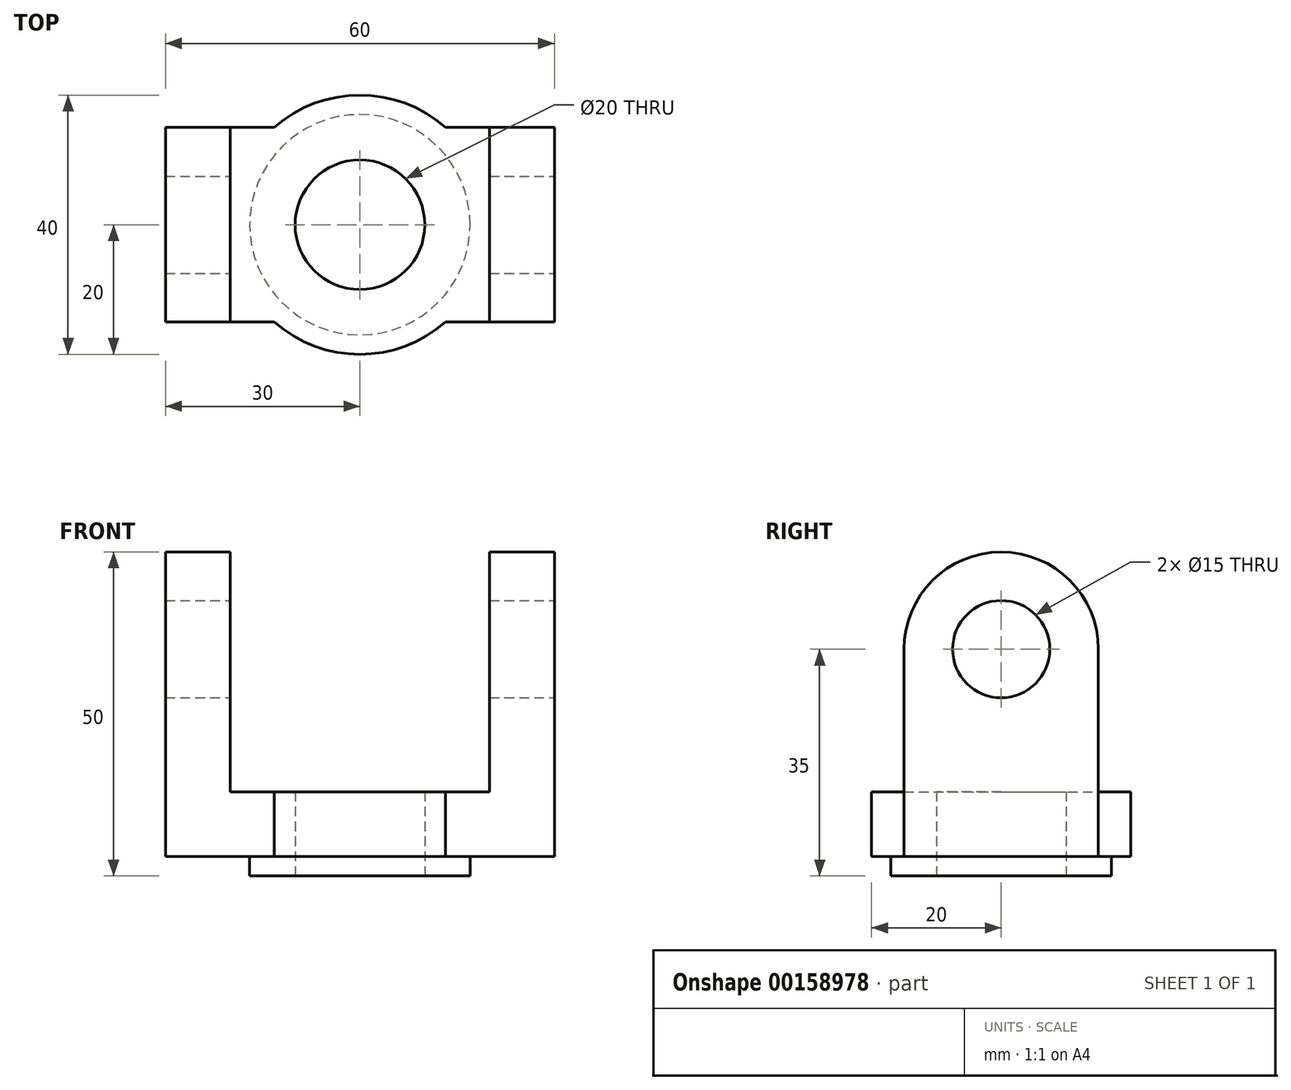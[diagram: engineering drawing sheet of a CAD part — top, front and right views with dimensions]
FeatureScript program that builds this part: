
annotation { "Feature Type Name" : "Feature", "Feature Type Description" : "" }
export const myFeature = defineFeature(function(context is Context, id is Id, definition is map)
    precondition{}
    {
        {
            var Q0;
            Q0=qCreatedBy(makeId("Front.planeOp"),FACE);
            var sketch = newSketch(context, id + "F0", { "sketchPlane" : qUnion([Q0])});
            skLineSegment(sketch, "E0.bottom", {"start": v(0, 0) * mm, "end": v(60, 0) * mm});
            skLineSegment(sketch, "E0.top", {"start": v(0, 47.5) * mm, "end": v(60, 47.5) * mm});
            skLineSegment(sketch, "E0.left", {"start": v(0, 0) * mm, "end": v(0, 47.5) * mm});
            skLineSegment(sketch, "E0.right", {"start": v(60, 0) * mm, "end": v(60, 47.5) * mm});
            skSolve(sketch);
        }
        {
            var Q0;
            Q0 = qSketchRegion(id + "F0", true);
            extrude(context, id + "F1", {"entities" : qUnion([Q0]), "depth" : 40 * mm});
        }
        {
            var Q0;
            Q0=qCreatedBy(makeId("Front.planeOp"),FACE);
            var sketch = newSketch(context, id + "F2", { "sketchPlane" : qUnion([Q0])});
            skLineSegment(sketch, "E1.bottom", {"start": v(10, 47.5) * mm, "end": v(50, 47.5) * mm});
            skLineSegment(sketch, "E1.top", {"start": v(10, 10) * mm, "end": v(50, 10) * mm});
            skLineSegment(sketch, "E1.left", {"start": v(10, 47.5) * mm, "end": v(10, 10) * mm});
            skLineSegment(sketch, "E1.right", {"start": v(50, 47.5) * mm, "end": v(50, 10) * mm});
            skSolve(sketch);
        }
        {
            var Q0;
            Q0 = qSketchRegion(id + "F2", true);
            extrude(context, id + "F3", {"entities" : qUnion([Q0]), "operationType" : NewBodyOperationType.REMOVE, "depth" : 40 * mm});
        }
        {
            var Q0;
            Q0=makeQuery(id+"F1.opExtrude","SWEPT_FACE",FACE,{"disambiguationData":[OSD([sQuery(id+"F0.wireOp",EDGE,"E0.bottom")])]});
            var sketch = newSketch(context, id + "F4", { "sketchPlane" : qUnion([Q0])});
            skCircle(sketch, "E2", {"center": v(30, 20) * mm, "radius": 17 * mm});
            skLineSegment(sketch, "E3", {"start": v(0, 20) * mm, "end": v(60, 20) * mm, "construction": true});
            skLineSegment(sketch, "E4", {"start": v(30, 40) * mm, "end": v(30, 0) * mm, "construction": true});
            skSolve(sketch);
        }
        {
            var Q0;
            Q0 = qSketchRegion(id + "F4", true);
            extrude(context, id + "F5", {"entities" : qUnion([Q0]), "operationType" : NewBodyOperationType.ADD, "depth" : 3 * mm});
        }
        {
            var Q0;
            Q0=makeQuery(id+"F1.opExtrude","SWEPT_FACE",FACE,{"disambiguationData":[OSD([sQuery(id+"F0.wireOp",EDGE,"E0.right")])]});
            var sketch = newSketch(context, id + "F6", { "sketchPlane" : qUnion([Q0])});
            skLineSegment(sketch, "E5.bottom", {"start": v(-35, 0) * mm, "end": v(-5, 0) * mm});
            skLineSegment(sketch, "E5.left", {"start": v(-35, 0) * mm, "end": v(-35, 32) * mm});
            skLineSegment(sketch, "E5.right", {"start": v(-5, 0) * mm, "end": v(-5, 32) * mm});
            skArc(sketch, "E6", {"start": v(-5, 32) * mm, "mid": v(-20, 47) * mm, "end": v(-35, 32) * mm});
            skCircle(sketch, "E7", {"center": v(-20, 32) * mm, "radius": 7.5 * mm});
            skLineSegment(sketch, "E8", {"start": v(-35, 32) * mm, "end": v(-5, 32) * mm, "construction": true});
            skPoint(sketch, "E9", {"position": v(-20, 47) * mm});
            skSolve(sketch);
        }
        {
            var Q0;
            {var subQ3=sQuery(id+"F6.wireOp",EDGE,"E5.left");Q0=makeQuery(id+"F6.imprint","IMPRINT",FACE,{"disambiguationData":[TD([[makeQuery(id+"F6.imprint","IMPRINT",EDGE,{"derivedFrom":subQ3}),1.0]])]});}
            var sketch = newSketch(context, id + "F7", { "sketchPlane" : qUnion([Q0])});
            skLineSegment(sketch, "E10", {"start": v(-35, 0) * mm, "end": v(-40, 0) * mm});
            skLineSegment(sketch, "E11", {"start": v(-40, 0) * mm, "end": v(-40, 47.5) * mm});
            skLineSegment(sketch, "E12", {"start": v(-40, 47.5) * mm, "end": v(-19.67, 47.5) * mm});
            skLineSegment(sketch, "E13", {"start": v(-35, 0) * mm, "end": v(-35, 32) * mm});
            skLineSegment(sketch, "E14", {"start": v(-19.67, 47.5) * mm, "end": v(0, 47.5) * mm});
            skLineSegment(sketch, "E15", {"start": v(0, 47.5) * mm, "end": v(0, 0) * mm});
            skLineSegment(sketch, "E16", {"start": v(0, 0) * mm, "end": v(-5, 0) * mm});
            skLineSegment(sketch, "E17", {"start": v(-5, 0) * mm, "end": v(-5, 32) * mm});
            skArc(sketch, "E18", {"start": v(-35, 32) * mm, "mid": v(-20, 47) * mm, "end": v(-5, 32) * mm});
            skSolve(sketch);
        }
        {
            var Q0;
            Q0 = qSketchRegion(id + "F7", true);
            extrude(context, id + "F8", {"entities" : qUnion([Q0]), "operationType" : NewBodyOperationType.REMOVE, "endBound" : BoundingType.THROUGH_ALL, "oppositeDirection" : true, "depth" : 25 * mm});
        }
        {
            var Q0;
            Q0=makeQuery(id+"F6.imprint","IMPRINT",FACE,{"disambiguationData":[TD([[makeQuery(id+"F6.imprint","IMPRINT",EDGE,{"derivedFrom":sQuery(id+"F6.wireOp",EDGE,"E5.bottom")}),1.0]])]});
            var sketch = newSketch(context, id + "F9", { "sketchPlane" : qUnion([Q0])});
            skLineSegment(sketch, "E19", {"start": v(-35, 32) * mm, "end": v(-5, 32) * mm, "construction": true});
            skCircle(sketch, "E20", {"center": v(-20, 32) * mm, "radius": 7.5 * mm});
            skSolve(sketch);
        }
        {
            var Q0;
            Q0 = qSketchRegion(id + "F9", true);
            extrude(context, id + "F10", {"entities" : qUnion([Q0]), "operationType" : NewBodyOperationType.REMOVE, "endBound" : BoundingType.THROUGH_ALL, "oppositeDirection" : true, "depth" : 25 * mm});
        }
        {
            var Q0;
            Q0=qCreatedBy(makeId("Top.planeOp"),FACE);
            var sketch = newSketch(context, id + "F11", { "sketchPlane" : qUnion([Q0])});
            skLineSegment(sketch, "E21", {"start": v(60, -20) * mm, "end": v(0, -20) * mm, "construction": true});
            skLineSegment(sketch, "E22", {"start": v(30, -5) * mm, "end": v(30, -35) * mm, "construction": true});
            skCircle(sketch, "E23", {"center": v(30, -20) * mm, "radius": 10 * mm});
            skSolve(sketch);
        }
        {
            var Q0;
            Q0 = qSketchRegion(id + "F11", true);
            extrude(context, id + "F12", {"entities" : qUnion([Q0]), "operationType" : NewBodyOperationType.REMOVE, "endBound" : BoundingType.THROUGH_ALL, "depth" : 30 * mm});
        }
        {
            var Q0;
            Q0=makeQuery(id+"F3.boolean.opBoolean","COPY",FACE,{"derivedFrom":makeQuery(id+"F3.opExtrude","SWEPT_FACE",FACE,{"disambiguationData":[OSD([sQuery(id+"F2.wireOp",EDGE,"E1.top")])]})});
            var sketch = newSketch(context, id + "F13", { "sketchPlane" : qUnion([Q0])});
            skLineSegment(sketch, "E24", {"start": v(0, -20) * mm, "end": v(60, -20) * mm, "construction": true});
            skPoint(sketch, "E25", {"position": v(12.96, -20) * mm});
            skPoint(sketch, "E26", {"position": v(47.1, -20) * mm});
            skArc(sketch, "E27", {"start": v(43.23, -5) * mm, "mid": v(30, 0) * mm, "end": v(16.77, -5) * mm});
            skArc(sketch, "E28", {"start": v(16.77, -35) * mm, "mid": v(30, -40) * mm, "end": v(43.23, -35) * mm});
            skLineSegment(sketch, "E29", {"start": v(16.77, -35) * mm, "end": v(43.23, -35) * mm});
            skLineSegment(sketch, "E30", {"start": v(10, -5) * mm, "end": v(50, -5) * mm});
            skPoint(sketch, "E31", {"position": v(30, -5) * mm});
            skSolve(sketch);
        }
        {
            var Q0;
            Q0=makeQuery(id+"F5.opExtrude","CAP_FACE",FACE,{"disambiguationData":[OSD([sQuery(id+"F4.wireOp",EDGE,"E2")])],"isStart":false});
            var sketch = newSketch(context, id + "F14", { "sketchPlane" : qUnion([Q0])});
            skCircle(sketch, "E32", {"center": v(30, 20) * mm, "radius": 10 * mm});
            skSolve(sketch);
        }
        {
            var Q0;
            Q0 = qSketchRegion(id + "F14", true);
            extrude(context, id + "F15", {"entities" : qUnion([Q0]), "operationType" : NewBodyOperationType.REMOVE, "oppositeDirection" : true, "depth" : 25 * mm});
        }
        {
            var Q0;
            Q0 = qSketchRegion(id + "F13", true);
            extrude(context, id + "F16", {"entities" : qUnion([Q0]), "operationType" : NewBodyOperationType.ADD, "oppositeDirection" : true, "depth" : 10 * mm});
        }
    });
